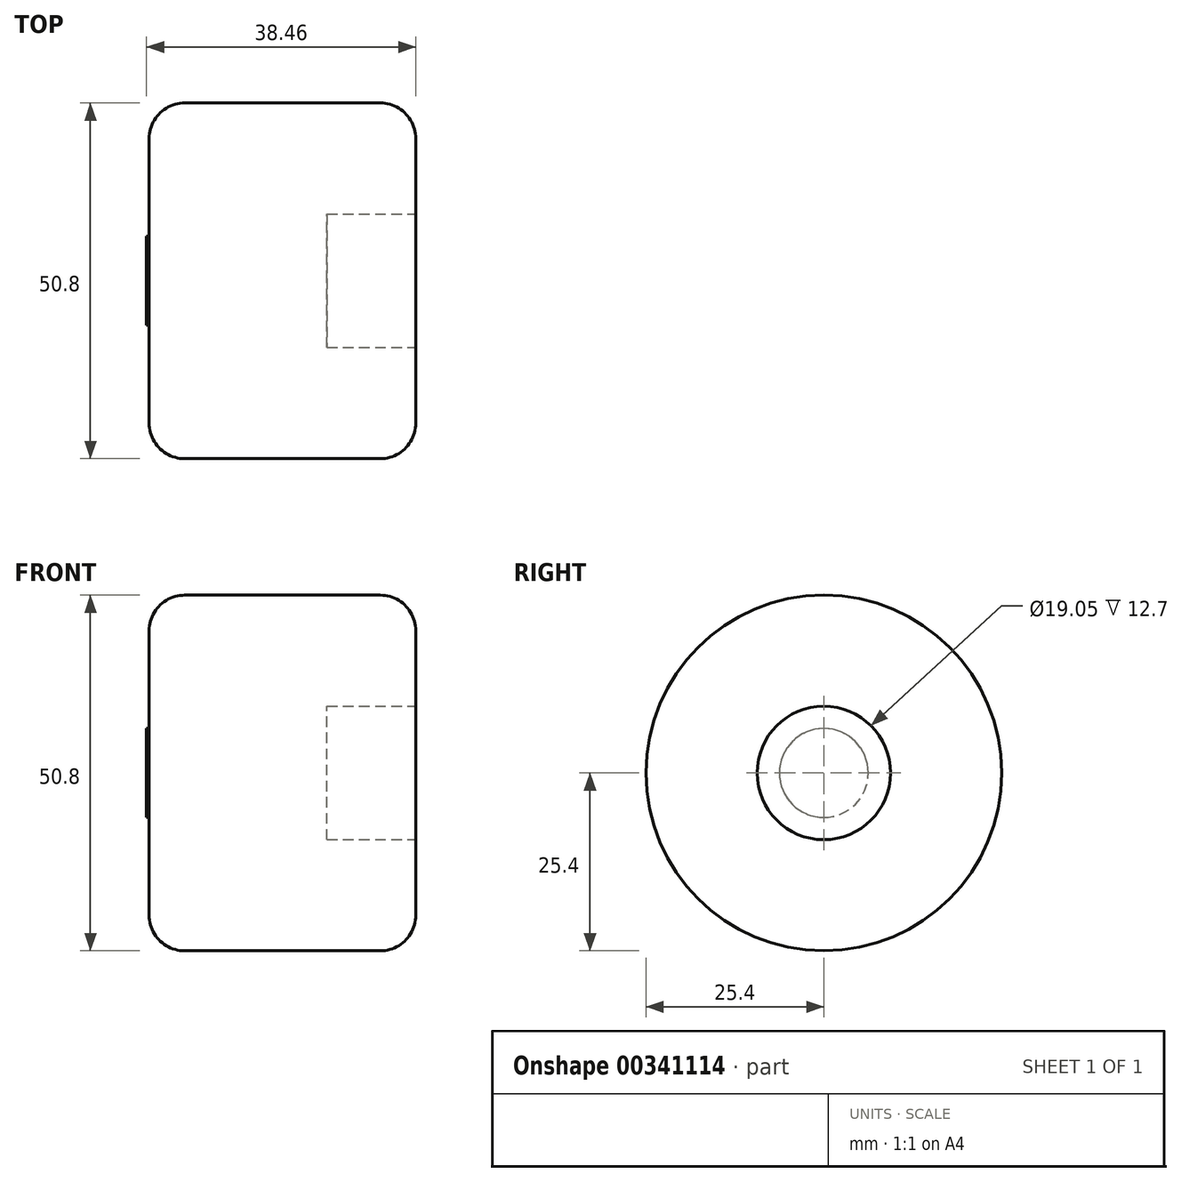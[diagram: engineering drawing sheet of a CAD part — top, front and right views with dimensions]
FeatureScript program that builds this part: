
annotation { "Feature Type Name" : "Feature", "Feature Type Description" : "" }
export const myFeature = defineFeature(function(context is Context, id is Id, definition is map)
    precondition{}
    {
        {
            var Q0;
            Q0=qCreatedBy(makeId("Right.planeOp"),FACE);
            var sketch = newSketch(context, id + "F0", { "sketchPlane" : qUnion([Q0])});
            skCircle(sketch, "E0", {"center": v(0, 0) * mm, "radius": 6.35 * mm});
            skSolve(sketch);
        }
        {
            var Q0;
            Q0=makeQuery(id+"F0.imprint","IMPRINT",FACE,{"disambiguationData":[TD([[makeQuery(id+"F0.imprint","IMPRINT",EDGE,{"derivedFrom":sQuery(id+"F0.wireOp",EDGE,"E0")}),1.0]])]});
            extrude(context, id + "F1", {"entities" : qUnion([Q0]), "depth" : 25.4 * mm});
        }
        {
            var Q0;
            Q0=makeQuery(id+"F1.opExtrude","CAP_FACE",FACE,{"disambiguationData":[OSD([sQuery(id+"F0.wireOp",EDGE,"E0")])],"isStart":false});
            var sketch = newSketch(context, id + "F2", { "sketchPlane" : qUnion([Q0])});
            skCircle(sketch, "E1", {"center": v(0, 0) * mm, "radius": 25.4 * mm});
            skSolve(sketch);
        }
        {
            var Q0;
            Q0=qSketchRegion(id+"F2",true);
            extrude(context, id + "F3", {"entities" : qUnion([Q0]), "operationType" : NewBodyOperationType.ADD, "depth" : 38.1 * mm});
        }
        {
            var Q0;
            Q0=makeQuery(id+"F3.opExtrude","CAP_FACE",FACE,{"disambiguationData":[OSD([sQuery(id+"F2.wireOp",EDGE,"E1")])],"isStart":false});
            var sketch = newSketch(context, id + "F4", { "sketchPlane" : qUnion([Q0])});
            skCircle(sketch, "E2", {"center": v(0, 0) * mm, "radius": 9.53 * mm});
            skSolve(sketch);
        }
        {
            var Q0;
            Q0=makeQuery(id+"F4.imprint","IMPRINT",FACE,{"disambiguationData":[TD([[makeQuery(id+"F4.imprint","IMPRINT",EDGE,{"derivedFrom":sQuery(id+"F4.wireOp",EDGE,"E2")}),1.0]])]});
            extrude(context, id + "F5", {"entities" : qUnion([Q0]), "operationType" : NewBodyOperationType.REMOVE, "oppositeDirection" : true, "depth" : 12.7 * mm});
        }
        {
            var Q0;
            Q0=makeQuery(id+"F3.opExtrude","CAP_EDGE",EDGE,{"disambiguationData":[OSD([sQuery(id+"F2.wireOp",EDGE,"E1")])],"isStart":false});
            var Q1;
            Q1=makeQuery(id+"F5.boolean.opBoolean","COPY",EDGE,{"derivedFrom":makeQuery(id+"F5.opExtrude","CAP_EDGE",EDGE,{"disambiguationData":[OSD([sQuery(id+"F4.wireOp",EDGE,"E2")])],"isStart":true})});
            var Q2;
            Q2=makeQuery(id+"F3.opExtrude","CAP_EDGE",EDGE,{"disambiguationData":[OSD([sQuery(id+"F2.wireOp",EDGE,"E1")])],"isStart":true});
            fillet(context, id + "F6", {"entities" : qUnion([Q0, Q1, Q2]), "radius" : 5.08 * mm, "tangentPropagation" : true, "allowEdgeOverflow" : false});
        }
        {
            var Q0;
            Q0=qCreatedBy(makeId("Front.planeOp"),FACE);
            var sketch = newSketch(context, id + "F7", { "sketchPlane" : qUnion([Q0])});
            skLineSegment(sketch, "E3.bottom", {"start": v(-13.81, -10.07) * mm, "end": v(25.04, -10.07) * mm});
            skLineSegment(sketch, "E3.top", {"start": v(-13.81, 19.57) * mm, "end": v(25.04, 19.57) * mm});
            skLineSegment(sketch, "E3.left", {"start": v(-13.81, -10.07) * mm, "end": v(-13.81, 19.57) * mm});
            skLineSegment(sketch, "E3.right", {"start": v(25.04, -10.07) * mm, "end": v(25.04, 19.57) * mm});
            skSolve(sketch);
        }
        {
            var Q0;
            Q0=makeQuery(id+"F7.imprint","IMPRINT",FACE,{"disambiguationData":[TD([[makeQuery(id+"F7.imprint","IMPRINT",EDGE,{"derivedFrom":sQuery(id+"F7.wireOp",EDGE,"E3.bottom")}),1.0]])]});
            extrude(context, id + "F8", {"entities" : qUnion([Q0]), "operationType" : NewBodyOperationType.ADD, "depth" : 25.4 * mm});
        }
        {
            var Q0;
            Q0=makeQuery(id+"F8.opExtrude","CAP_FACE",FACE,{"disambiguationData":[OSD([sQuery(id+"F7.wireOp",EDGE,"E3.bottom"),sQuery(id+"F7.wireOp",EDGE,"E3.top"),sQuery(id+"F7.wireOp",EDGE,"E3.left"),sQuery(id+"F7.wireOp",EDGE,"E3.right")])],"isStart":true});
            extrude(context, id + "F9", {"entities" : qUnion([Q0]), "operationType" : NewBodyOperationType.ADD, "depth" : 25.4 * mm});
        }
        {
            var Q0;
            Q0=makeQuery(id+"F9.opExtrude","CAP_FACE",FACE,{"disambiguationData":[OSD([sQuery(id+"F7.wireOp",EDGE,"E3.bottom"),sQuery(id+"F7.wireOp",EDGE,"E3.top"),sQuery(id+"F7.wireOp",EDGE,"E3.left"),sQuery(id+"F7.wireOp",EDGE,"E3.right")])],"isStart":false});
            extrude(context, id + "F10", {"entities" : qUnion([Q0]), "operationType" : NewBodyOperationType.REMOVE, "oppositeDirection" : true, "depth" : 25.4 * mm});
        }
        {
            var Q0;
            Q0=makeQuery(id+"F8.opExtrude","CAP_FACE",FACE,{"disambiguationData":[OSD([sQuery(id+"F7.wireOp",EDGE,"E3.bottom"),sQuery(id+"F7.wireOp",EDGE,"E3.top"),sQuery(id+"F7.wireOp",EDGE,"E3.left"),sQuery(id+"F7.wireOp",EDGE,"E3.right")])],"isStart":false});
            extrude(context, id + "F11", {"entities" : qUnion([Q0]), "operationType" : NewBodyOperationType.REMOVE, "oppositeDirection" : true, "depth" : 56.13 * mm});
        }
    });
